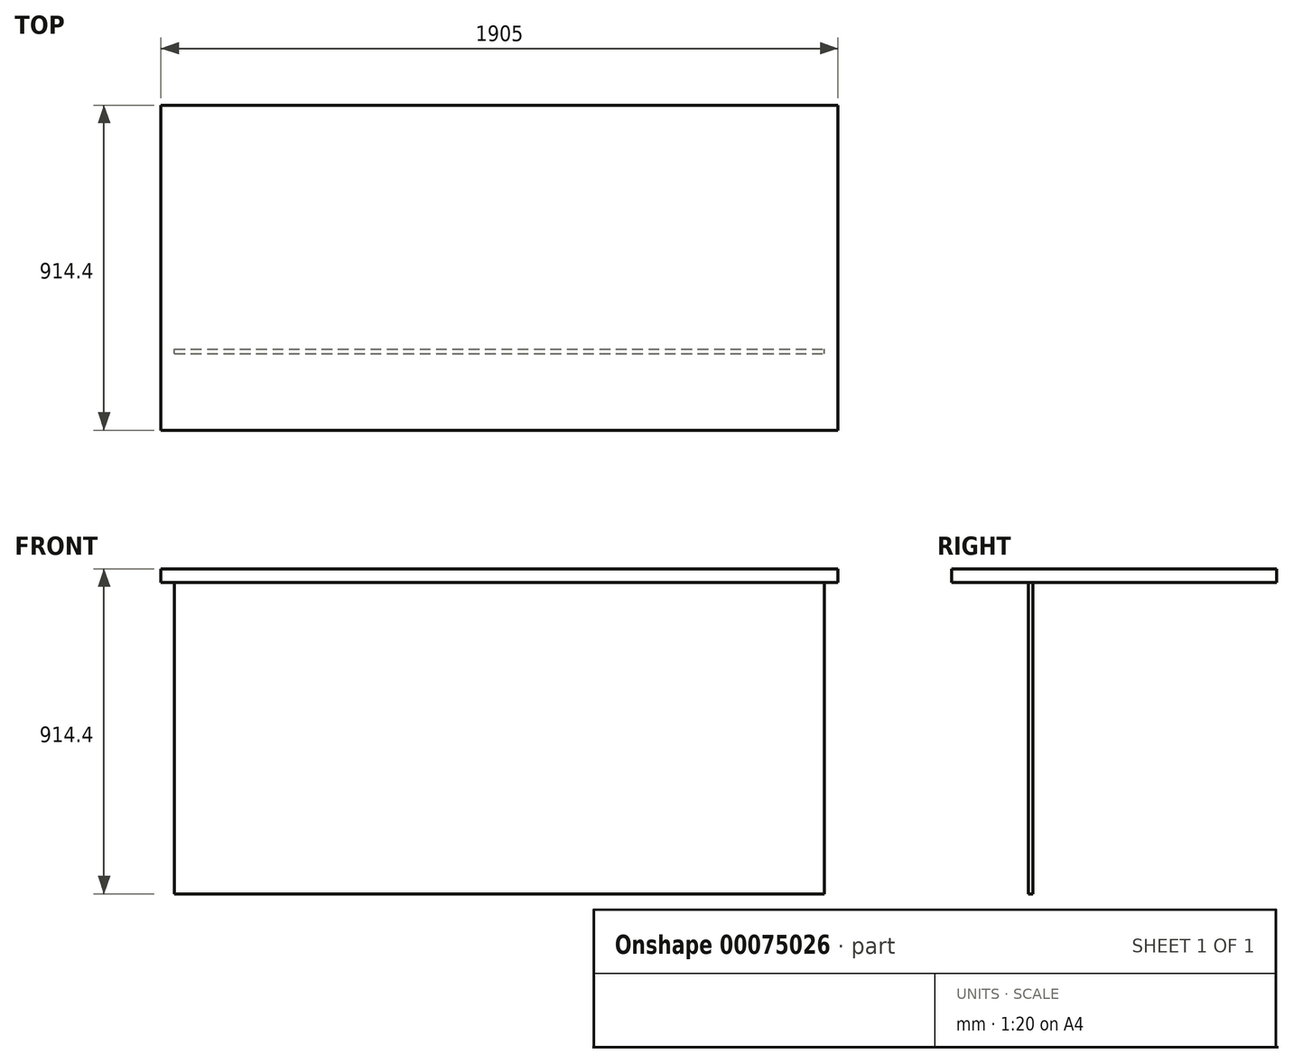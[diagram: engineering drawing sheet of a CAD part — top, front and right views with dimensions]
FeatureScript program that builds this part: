
annotation { "Feature Type Name" : "Feature", "Feature Type Description" : "" }
export const myFeature = defineFeature(function(context is Context, id is Id, definition is map)
    precondition{}
    {
        {
            var Q0;
            Q0=qCreatedBy(makeId("Top.planeOp"),FACE);
            var sketch = newSketch(context, id + "F0", { "sketchPlane" : qUnion([Q0])});
            skLineSegment(sketch, "E0.rect.bottom", {"start": v(914.4, 457.2) * mm, "end": v(-914.4, 457.2) * mm});
            skLineSegment(sketch, "E0.rect.top", {"start": v(914.4, -457.2) * mm, "end": v(-914.4, -457.2) * mm});
            skLineSegment(sketch, "E0.rect.left", {"start": v(914.4, 457.2) * mm, "end": v(914.4, -457.2) * mm});
            skLineSegment(sketch, "E0.rect.right", {"start": v(-914.4, 457.2) * mm, "end": v(-914.4, -457.2) * mm});
            skPoint(sketch, "E0.rect.middle", {"position": v(0, 0) * mm});
            skLineSegment(sketch, "E1.bottom", {"start": v(-914.4, 457.2) * mm, "end": v(-952.5, 457.2) * mm});
            skLineSegment(sketch, "E1.top", {"start": v(-914.4, -457.2) * mm, "end": v(-952.5, -457.2) * mm});
            skLineSegment(sketch, "E1.right", {"start": v(-952.5, 457.2) * mm, "end": v(-952.5, -457.2) * mm});
            skLineSegment(sketch, "E2.bottom", {"start": v(914.4, 457.2) * mm, "end": v(952.5, 457.2) * mm});
            skLineSegment(sketch, "E2.top", {"start": v(914.4, -457.2) * mm, "end": v(952.5, -457.2) * mm});
            skLineSegment(sketch, "E2.right", {"start": v(952.5, 457.2) * mm, "end": v(952.5, -457.2) * mm});
            skSolve(sketch);
        }
        {
            var Q0;
            Q0=makeQuery(id+"F0.imprint","IMPRINT",FACE,{"disambiguationData":[TD([[makeQuery(id+"F0.imprint","IMPRINT",EDGE,{"derivedFrom":sQuery(id+"F0.wireOp",EDGE,"E1.bottom")}),1.0]])]});
            var Q1;
            Q1=makeQuery(id+"F0.imprint","IMPRINT",FACE,{"disambiguationData":[TD([[makeQuery(id+"F0.imprint","IMPRINT",EDGE,{"derivedFrom":sQuery(id+"F0.wireOp",EDGE,"E0.rect.bottom")}),1.0]])]});
            var Q2;
            Q2=makeQuery(id+"F0.imprint","IMPRINT",FACE,{"disambiguationData":[TD([[makeQuery(id+"F0.imprint","IMPRINT",EDGE,{"derivedFrom":sQuery(id+"F0.wireOp",EDGE,"E2.bottom")}),-1.0]])]});
            extrude(context, id + "F1", {"entities" : qUnion([Q0, Q1, Q2]), "depth" : 38.1 * mm});
        }
        {
            var Q0;
            Q0=makeQuery(id+"F0.imprint","IMPRINT",FACE,{"disambiguationData":[TD([[makeQuery(id+"F0.imprint","IMPRINT",EDGE,{"derivedFrom":sQuery(id+"F0.wireOp",EDGE,"E1.bottom")}),1.0]])]});
            var Q1;
            Q1=makeQuery(id+"F0.imprint","IMPRINT",FACE,{"disambiguationData":[TD([[makeQuery(id+"F0.imprint","IMPRINT",EDGE,{"derivedFrom":sQuery(id+"F0.wireOp",EDGE,"E2.bottom")}),-1.0]])]});
            extrude(context, id + "F2", {"entities" : qUnion([Q0, Q1]), "operationType" : NewBodyOperationType.ADD, "oppositeDirection" : true, "depth" : 876.3 * mm});
        }
        {
            var Q0;
            {var subQ0=sQuery(id+"F0.wireOp",EDGE,"E2.top");var subQ1=sQuery(id+"F0.wireOp",EDGE,"E1.top");Q0=makeQuery(id+"F2.boolean.opBoolean","MERGE",FACE,{"derivedFrom":[makeQuery(id+"F1.opExtrude","SWEPT_FACE",FACE,{"disambiguationData":[OSD([sQuery(id+"F0.wireOp",EDGE,"E0.rect.top"),subQ1,subQ0])]}),makeQuery(id+"F2.opExtrude","SWEPT_FACE",FACE,{"disambiguationData":[OSD([subQ1])]}),makeQuery(id+"F2.opExtrude","SWEPT_FACE",FACE,{"disambiguationData":[OSD([subQ0])]})]});}
            cPlane(context, id + "F3", {"entities" : qUnion([Q0]), "cplaneType" : CPlaneType.OFFSET, "offset" : 228.6 * mm, "oppositeDirection" : true, "width" : 152.4 * mm, "height" : 152.4 * mm});
        }
        {
            var Q0;
            Q0=qCreatedBy(id+"F3.planeOp",FACE);
            var sketch = newSketch(context, id + "F4", { "sketchPlane" : qUnion([Q0])});
            skLineSegment(sketch, "E3.bottom", {"start": v(-914.4, 0) * mm, "end": v(914.4, 0) * mm});
            skLineSegment(sketch, "E3.top", {"start": v(-914.4, -876.3) * mm, "end": v(914.4, -876.3) * mm});
            skLineSegment(sketch, "E3.left", {"start": v(-914.4, 0) * mm, "end": v(-914.4, -876.3) * mm});
            skLineSegment(sketch, "E3.right", {"start": v(914.4, 0) * mm, "end": v(914.4, -876.3) * mm});
            skSolve(sketch);
        }
        {
            var Q0;
            Q0=qSketchRegion(id+"F4",true);
            extrude(context, id + "F5", {"entities" : qUnion([Q0]), "depth" : 12.7 * mm});
        }
        {
            var Q0;
            {var subQ0=sQuery(id+"F0.wireOp",EDGE,"E2.right");Q0=makeQuery(id+"F2.boolean.opBoolean","MERGE",FACE,{"derivedFrom":[makeQuery(id+"F1.opExtrude","SWEPT_FACE",FACE,{"disambiguationData":[OSD([subQ0])]}),makeQuery(id+"F2.opExtrude","SWEPT_FACE",FACE,{"disambiguationData":[OSD([subQ0])]})]});}
            var sketch = newSketch(context, id + "F6", { "sketchPlane" : qUnion([Q0])});
            skLineSegment(sketch, "E4.bottom", {"start": v(-457.2, -876.3) * mm, "end": v(457.2, -876.3) * mm});
            skLineSegment(sketch, "E4.top", {"start": v(-457.2, 0) * mm, "end": v(457.2, 0) * mm});
            skLineSegment(sketch, "E4.left", {"start": v(-457.2, -876.3) * mm, "end": v(-457.2, 0) * mm});
            skLineSegment(sketch, "E4.right", {"start": v(457.2, -876.3) * mm, "end": v(457.2, 0) * mm});
            skSolve(sketch);
        }
        {
            var Q0;
            Q0=qSketchRegion(id+"F6",true);
            extrude(context, id + "F7", {"entities" : qUnion([Q0]), "operationType" : NewBodyOperationType.REMOVE, "oppositeDirection" : true, "depth" : 38.1 * mm});
        }
        {
            var Q0;
            {var subQ0=sQuery(id+"F0.wireOp",EDGE,"E1.right");Q0=makeQuery(id+"F2.boolean.opBoolean","MERGE",FACE,{"derivedFrom":[makeQuery(id+"F1.opExtrude","SWEPT_FACE",FACE,{"disambiguationData":[OSD([subQ0])]}),makeQuery(id+"F2.opExtrude","SWEPT_FACE",FACE,{"disambiguationData":[OSD([subQ0])]})]});}
            var sketch = newSketch(context, id + "F8", { "sketchPlane" : qUnion([Q0])});
            skLineSegment(sketch, "E5.bottom", {"start": v(-457.2, -876.3) * mm, "end": v(457.2, -876.3) * mm});
            skLineSegment(sketch, "E5.top", {"start": v(-457.2, 0) * mm, "end": v(457.2, 0) * mm});
            skLineSegment(sketch, "E5.left", {"start": v(-457.2, -876.3) * mm, "end": v(-457.2, 0) * mm});
            skLineSegment(sketch, "E5.right", {"start": v(457.2, -876.3) * mm, "end": v(457.2, 0) * mm});
            skSolve(sketch);
        }
        {
            var Q0;
            Q0=qSketchRegion(id+"F8",true);
            extrude(context, id + "F9", {"entities" : qUnion([Q0]), "operationType" : NewBodyOperationType.REMOVE, "oppositeDirection" : true, "depth" : 38.1 * mm});
        }
    });
